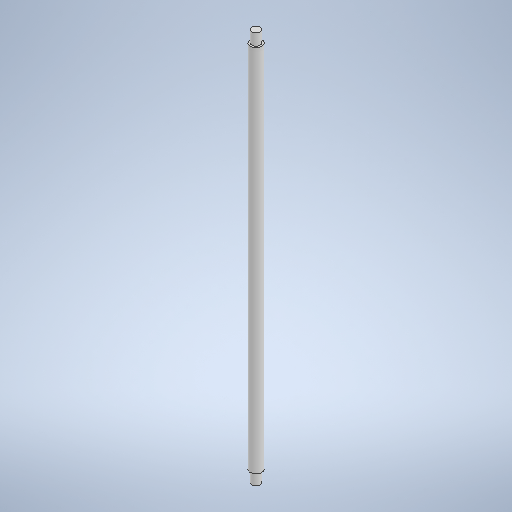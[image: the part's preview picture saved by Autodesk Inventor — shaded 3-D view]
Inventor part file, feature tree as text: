
AUTODESK INVENTOR PART (.ipt)
format: ipt  version: 2025.1 (Build 291241000, 241)  size: 257,536 bytes
history: native  units: mm
features: revolve x1, sketch x1
ambient origin geometry x8: Origin, YZ Plane, XZ Plane, XY Plane, X Axis, Y Axis, Z Axis, Center Point
bodies: Volumenkörper1 (feature_tree)
feature tree (2):
  revolve  "Umdrehung1"
  sketch  "Skizze1"  dims[d0=7.0mm d1=5.0mm d2=7.0mm d3=7.0mm d4=235.0mm d5=90.0deg]
